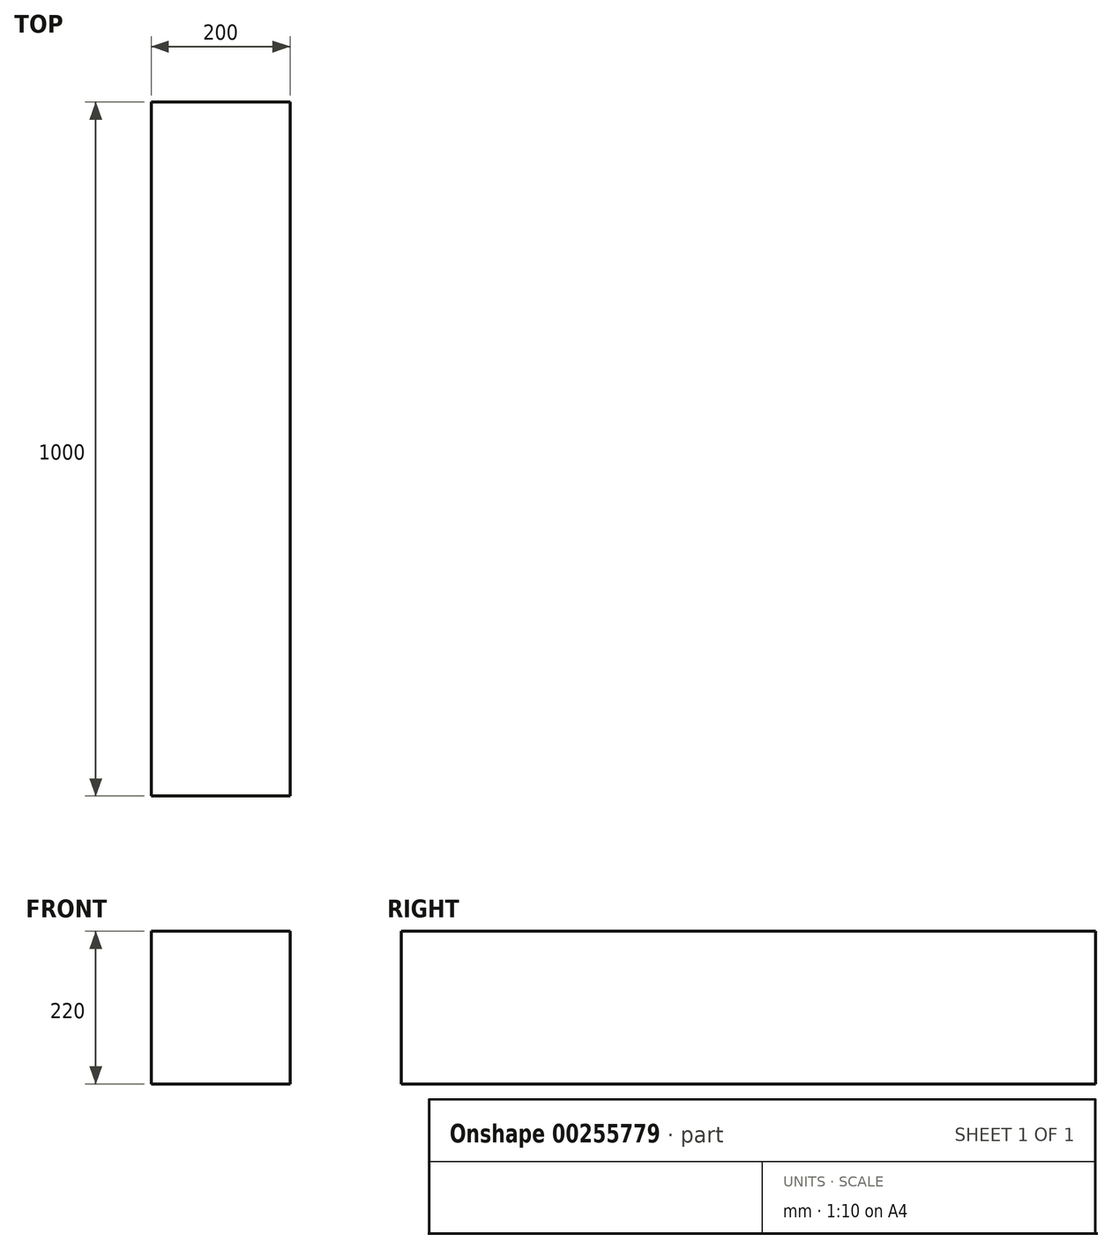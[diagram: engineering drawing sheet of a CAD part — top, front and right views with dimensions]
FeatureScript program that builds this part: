
annotation { "Feature Type Name" : "Feature", "Feature Type Description" : "" }
export const myFeature = defineFeature(function(context is Context, id is Id, definition is map)
    precondition{}
    {
        {
            var Q0;
            Q0=qCreatedBy(makeId("Front.planeOp"),FACE);
            var sketch = newSketch(context, id + "F0", { "sketchPlane" : qUnion([Q0])});
            skLineSegment(sketch, "E0.bottom", {"start": v(0, 0) * mm, "end": v(200, 0) * mm});
            skLineSegment(sketch, "E0.top", {"start": v(0, -220) * mm, "end": v(200, -220) * mm});
            skLineSegment(sketch, "E0.left", {"start": v(0, 0) * mm, "end": v(0, -220) * mm});
            skLineSegment(sketch, "E0.right", {"start": v(200, 0) * mm, "end": v(200, -220) * mm});
            skSolve(sketch);
        }
        {
            var Q0;
            Q0 = qSketchRegion(id + "F0", true);
            extrude(context, id + "F1", {"entities" : qUnion([Q0]), "endBound" : BoundingType.SYMMETRIC, "depth" : 1000 * mm});
        }
    });
